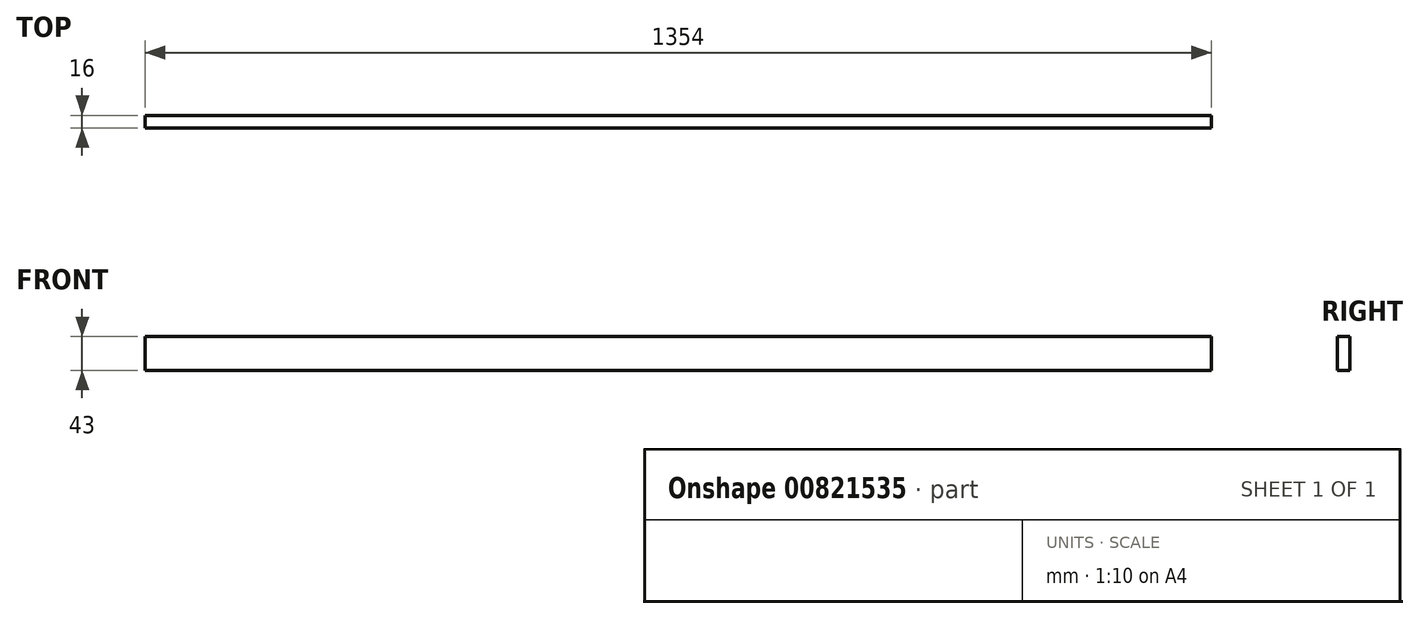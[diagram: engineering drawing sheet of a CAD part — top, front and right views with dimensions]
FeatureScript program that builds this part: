
annotation { "Feature Type Name" : "Feature", "Feature Type Description" : "" }
export const myFeature = defineFeature(function(context is Context, id is Id, definition is map)
    precondition{}
    {
        {
            var Q0;
            Q0=qCreatedBy(makeId("Front.planeOp"),FACE);
            var sketch = newSketch(context, id + "F0", { "sketchPlane" : qUnion([Q0])});
            skLineSegment(sketch, "E0.bottom", {"start": v(-677, 21.5) * mm, "end": v(677, 21.5) * mm});
            skLineSegment(sketch, "E0.top", {"start": v(-677, -21.5) * mm, "end": v(677, -21.5) * mm});
            skLineSegment(sketch, "E0.left", {"start": v(-677, 21.5) * mm, "end": v(-677, -21.5) * mm});
            skLineSegment(sketch, "E0.right", {"start": v(677, 21.5) * mm, "end": v(677, -21.5) * mm});
            skPoint(sketch, "E0.middle", {"position": v(0, 0) * mm});
            skSolve(sketch);
        }
        {
            var Q0;
            Q0=makeQuery(id+"F0.imprint","IMPRINT",FACE,{"disambiguationData":[TD([[makeQuery(id+"F0.imprint","IMPRINT",EDGE,{"derivedFrom":sQuery(id+"F0.wireOp",EDGE,"E0.bottom")}),-1.0]])]});
            extrude(context, id + "F1", {"entities" : qUnion([Q0]), "endBound" : BoundingType.SYMMETRIC, "depth" : 16 * mm, "offsetDistance" : 25 * mm});
        }
    });
